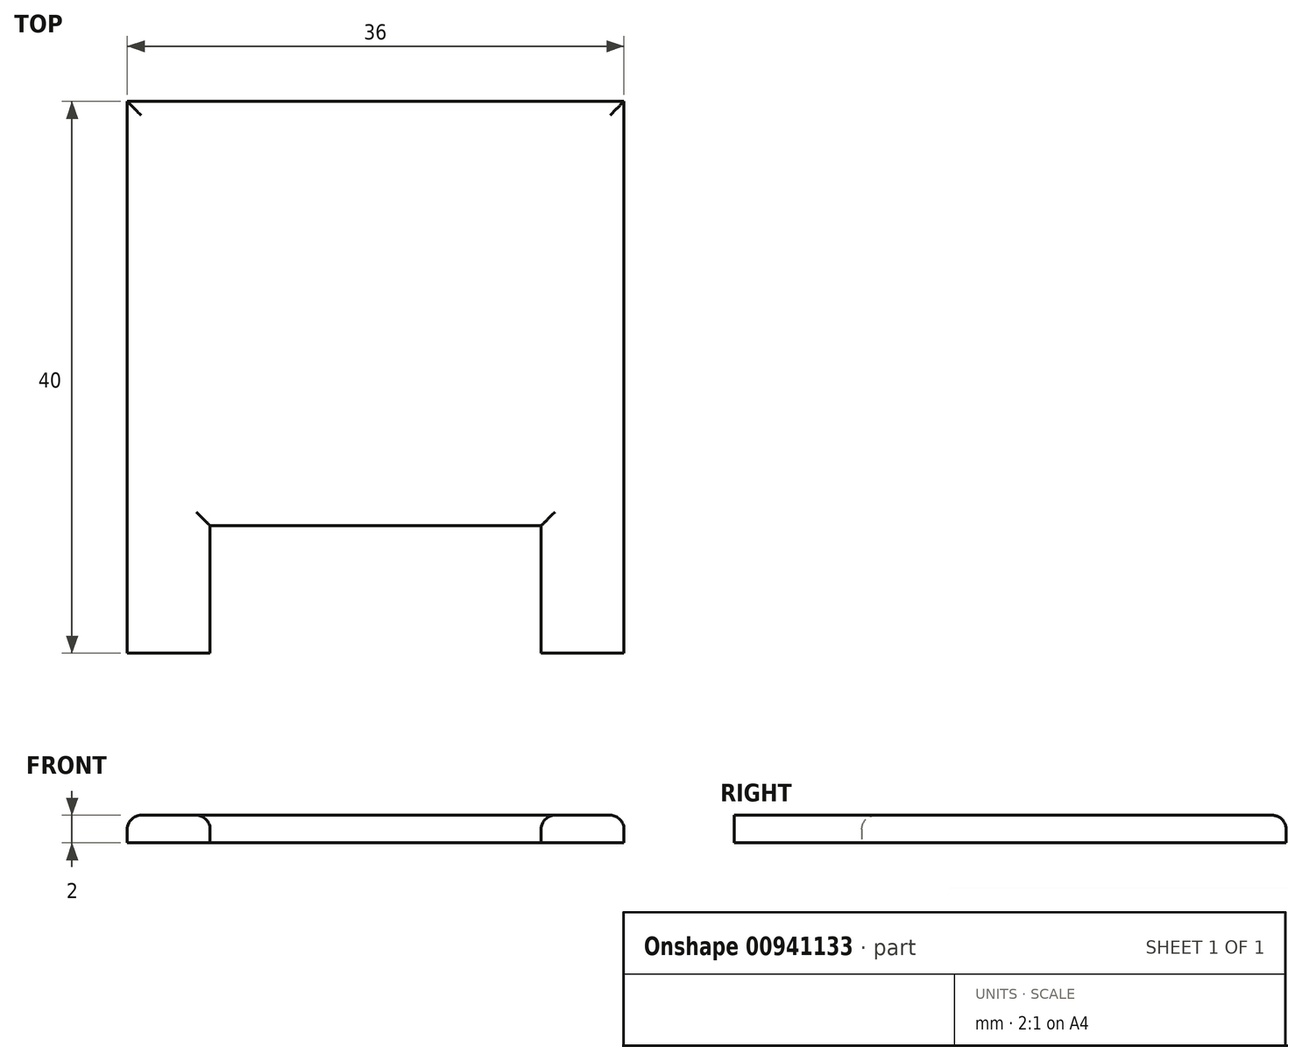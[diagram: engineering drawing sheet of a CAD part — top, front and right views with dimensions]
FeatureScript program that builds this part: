
annotation { "Feature Type Name" : "Feature", "Feature Type Description" : "" }
export const myFeature = defineFeature(function(context is Context, id is Id, definition is map)
    precondition{}
    {
        {
            var Q0;
            Q0=qCreatedBy(makeId("Top.planeOp"),FACE);
            var sketch = newSketch(context, id + "F0", { "sketchPlane" : qUnion([Q0])});
            skLineSegment(sketch, "E0", {"start": v(0, 18.35) * mm, "end": v(-18, 18.35) * mm});
            skLineSegment(sketch, "E1", {"start": v(-18, 18.35) * mm, "end": v(-18, -21.65) * mm});
            skLineSegment(sketch, "E2", {"start": v(-18, -21.65) * mm, "end": v(-12, -21.65) * mm});
            skLineSegment(sketch, "E3", {"start": v(-12, -21.65) * mm, "end": v(-12, -12.4) * mm});
            skLineSegment(sketch, "E4", {"start": v(-12, -12.4) * mm, "end": v(0, -12.4) * mm});
            skLineSegment(sketch, "E5.MirrorCS", {"start": v(0, 18.35) * mm, "end": v(18, 18.35) * mm});
            skLineSegment(sketch, "E6.MirrorCS", {"start": v(18, 18.35) * mm, "end": v(18, -21.65) * mm});
            skLineSegment(sketch, "E7.MirrorCS", {"start": v(18, -21.65) * mm, "end": v(12, -21.65) * mm});
            skLineSegment(sketch, "E8.MirrorCS", {"start": v(12, -21.65) * mm, "end": v(12, -12.4) * mm});
            skLineSegment(sketch, "E9.MirrorCS", {"start": v(12, -12.4) * mm, "end": v(0, -12.4) * mm});
            skSolve(sketch);
        }
        {
            var Q0;
            Q0 = qSketchRegion(id + "F0", true);
            var Q1;
            Q1=makeQuery(id+"F0.imprint","IMPRINT",FACE,{"disambiguationData":[TD([[makeQuery(id+"F0.imprint","IMPRINT",EDGE,{"derivedFrom":sQuery(id+"F0.wireOp",EDGE,"E0")}),1.0]])]});
            extrude(context, id + "F1", {"entities" : qUnion([Q0, Q1]), "depth" : 2 * mm, "offsetDistance" : 25 * mm});
        }
        {
            var Q0;
            Q0=makeQuery(id+"F1.opExtrude","CAP_EDGE",EDGE,{"disambiguationData":[OSD([sQuery(id+"F0.wireOp",EDGE,"E1")])],"isStart":false});
            var Q1;
            Q1=makeQuery(id+"F1.opExtrude","CAP_EDGE",EDGE,{"disambiguationData":[OSD([sQuery(id+"F0.wireOp",EDGE,"E6.MirrorCS")])],"isStart":false});
            var Q2;
            Q2=makeQuery(id+"F1.opExtrude","CAP_EDGE",EDGE,{"disambiguationData":[OSD([sQuery(id+"F0.wireOp",EDGE,"E8.MirrorCS")])],"isStart":false});
            var Q3;
            Q3=makeQuery(id+"F1.opExtrude","CAP_EDGE",EDGE,{"disambiguationData":[OSD([sQuery(id+"F0.wireOp",EDGE,"E4"),sQuery(id+"F0.wireOp",EDGE,"E9.MirrorCS")])],"isStart":false});
            var Q4;
            Q4=makeQuery(id+"F1.opExtrude","CAP_EDGE",EDGE,{"disambiguationData":[OSD([sQuery(id+"F0.wireOp",EDGE,"E3")])],"isStart":false});
            var Q5;
            Q5=makeQuery(id+"F1.opExtrude","CAP_EDGE",EDGE,{"disambiguationData":[OSD([sQuery(id+"F0.wireOp",EDGE,"E0"),sQuery(id+"F0.wireOp",EDGE,"E5.MirrorCS")])],"isStart":false});
            fillet(context, id + "F2", {"entities" : qUnion([Q0, Q1, Q2, Q3, Q4, Q5]), "radius" : 1 * mm, "tangentPropagation" : true, "allowEdgeOverflow" : false});
        }
    });
